# Revit family: Access_Door-Lightweight-Best Access Doors-Drywall Inlay-BA-IVH___1
name_source: partatom
category: Specialty Equipment
units: mm (PartAtom-declared; Revit-internal decimal feet)

## family parameters
Cut with Voids When Loaded = No
Host = Face
OmniClass Number = 23.30.10.27.17
OmniClass Title = Access Doors
Part Type = Normal
Room Calculation Point = No
Round Connector Dimension = Use Diameter
Shared = No

## types (1)
- Not a Type - Load Type Catalog
    A = 20 "
    Assembly Code = C1020700
    B = 20 "
    C = 22.2 "
    Construction Material = Metal - Best Access Doors - Aluminum
    D = 22.2 "
    Default Elevation = 0 "
    Description = BA-IVH Invisa Hatch Drywall Inlay with Fully Detachable Hatch
    Door Position = 0.37 "
    Drywall 1/2" = Yes
    Drywall 5/8" = No
    Drywall Size = 0.5 "
    E = 20.14 "
    F = 20.14 "
    Finish = Metal - Best Access Doors - Powder Coated White
    Height = 20 "
    Lock = No
    Manufacturer = Best Access Doors
    Product Documentation Link = https://www.bestaccessdoors.com
    Product Page URL = https://www.bestaccessdoors.com
    Product data url = https://bimobject.com
    Real Panel Height = 19.88 "
    Real Panel Width = 19.88 "
    URL = https://www.bestaccessdoors.com
    Width = 20 "

## geometry (parser evidence)
native form markers: Blend x2, Sweep x8
no freeform markers — native parametric forms only
